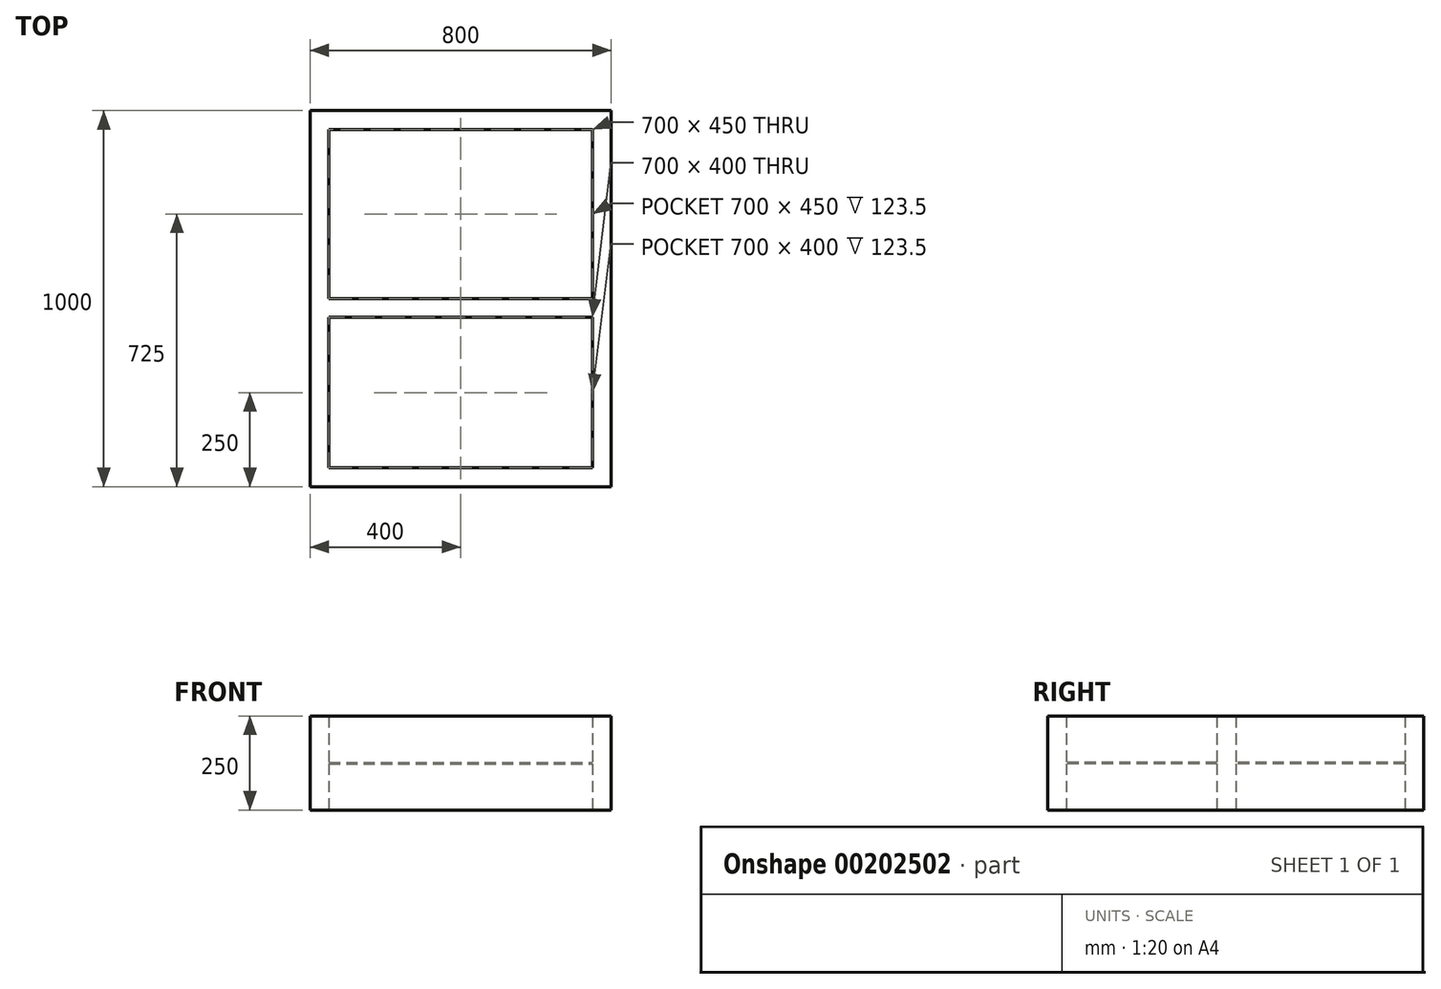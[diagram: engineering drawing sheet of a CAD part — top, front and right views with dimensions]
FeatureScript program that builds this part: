
annotation { "Feature Type Name" : "Feature", "Feature Type Description" : "" }
export const myFeature = defineFeature(function(context is Context, id is Id, definition is map)
    precondition{}
    {
        {
            var Q0;
            Q0=qCreatedBy(makeId("Top.planeOp"),FACE);
            var sketch = newSketch(context, id + "F0", { "sketchPlane" : qUnion([Q0])});
            skLineSegment(sketch, "E0.bottom", {"start": v(400, 500) * mm, "end": v(-400, 500) * mm});
            skLineSegment(sketch, "E0.top", {"start": v(400, -500) * mm, "end": v(-400, -500) * mm});
            skLineSegment(sketch, "E0.left", {"start": v(400, 500) * mm, "end": v(400, -500) * mm});
            skLineSegment(sketch, "E0.right", {"start": v(-400, 500) * mm, "end": v(-400, -500) * mm});
            skPoint(sketch, "E0.middle", {"position": v(0, 0) * mm});
            skLineSegment(sketch, "E1.bottom", {"start": v(-350, 450) * mm, "end": v(350, 450) * mm});
            skLineSegment(sketch, "E1.top", {"start": v(-350, 0) * mm, "end": v(350, 0) * mm});
            skLineSegment(sketch, "E1.left", {"start": v(-350, 450) * mm, "end": v(-350, 0) * mm});
            skLineSegment(sketch, "E1.right", {"start": v(350, 450) * mm, "end": v(350, 0) * mm});
            skLineSegment(sketch, "E2.bottom", {"start": v(-350, -50) * mm, "end": v(350, -50) * mm});
            skLineSegment(sketch, "E2.top", {"start": v(-350, -450) * mm, "end": v(350, -450) * mm});
            skLineSegment(sketch, "E2.left", {"start": v(-350, -50) * mm, "end": v(-350, -450) * mm});
            skLineSegment(sketch, "E2.right", {"start": v(350, -50) * mm, "end": v(350, -450) * mm});
            skSolve(sketch);
        }
        {
            var Q0;
            Q0=makeQuery(id+"F0.imprint","IMPRINT",FACE,{"disambiguationData":[TD([[makeQuery(id+"F0.imprint","IMPRINT",EDGE,{"derivedFrom":sQuery(id+"F0.wireOp",EDGE,"E0.bottom")}),1.0]])]});
            extrude(context, id + "F1", {"entities" : qUnion([Q0]), "endBound" : BoundingType.SYMMETRIC, "depth" : 250 * mm});
        }
        {
            var Q0;
            Q0=qCreatedBy(makeId("Top.planeOp"),FACE);
            var sketch = newSketch(context, id + "F2", { "sketchPlane" : qUnion([Q0])});
            skLineSegment(sketch, "E3.bottom", {"start": v(-350, 450) * mm, "end": v(350, 450) * mm});
            skLineSegment(sketch, "E3.top", {"start": v(-350, 0) * mm, "end": v(350, 0) * mm});
            skLineSegment(sketch, "E3.left", {"start": v(-350, 450) * mm, "end": v(-350, 0) * mm});
            skLineSegment(sketch, "E3.right", {"start": v(350, 450) * mm, "end": v(350, 0) * mm});
            skLineSegment(sketch, "E4.top", {"start": v(-350, -450) * mm, "end": v(350, -450) * mm});
            skLineSegment(sketch, "E4.left", {"start": v(-350, 0) * mm, "end": v(-350, -450) * mm});
            skLineSegment(sketch, "E4.right", {"start": v(350, 0) * mm, "end": v(350, -450) * mm});
            skSolve(sketch);
        }
        {
            var Q0;
            Q0=qSketchRegion(id+"F2",true);
            extrude(context, id + "F3", {"entities" : qUnion([Q0]), "operationType" : NewBodyOperationType.ADD, "endBound" : BoundingType.SYMMETRIC, "depth" : 3 * mm});
        }
    });
